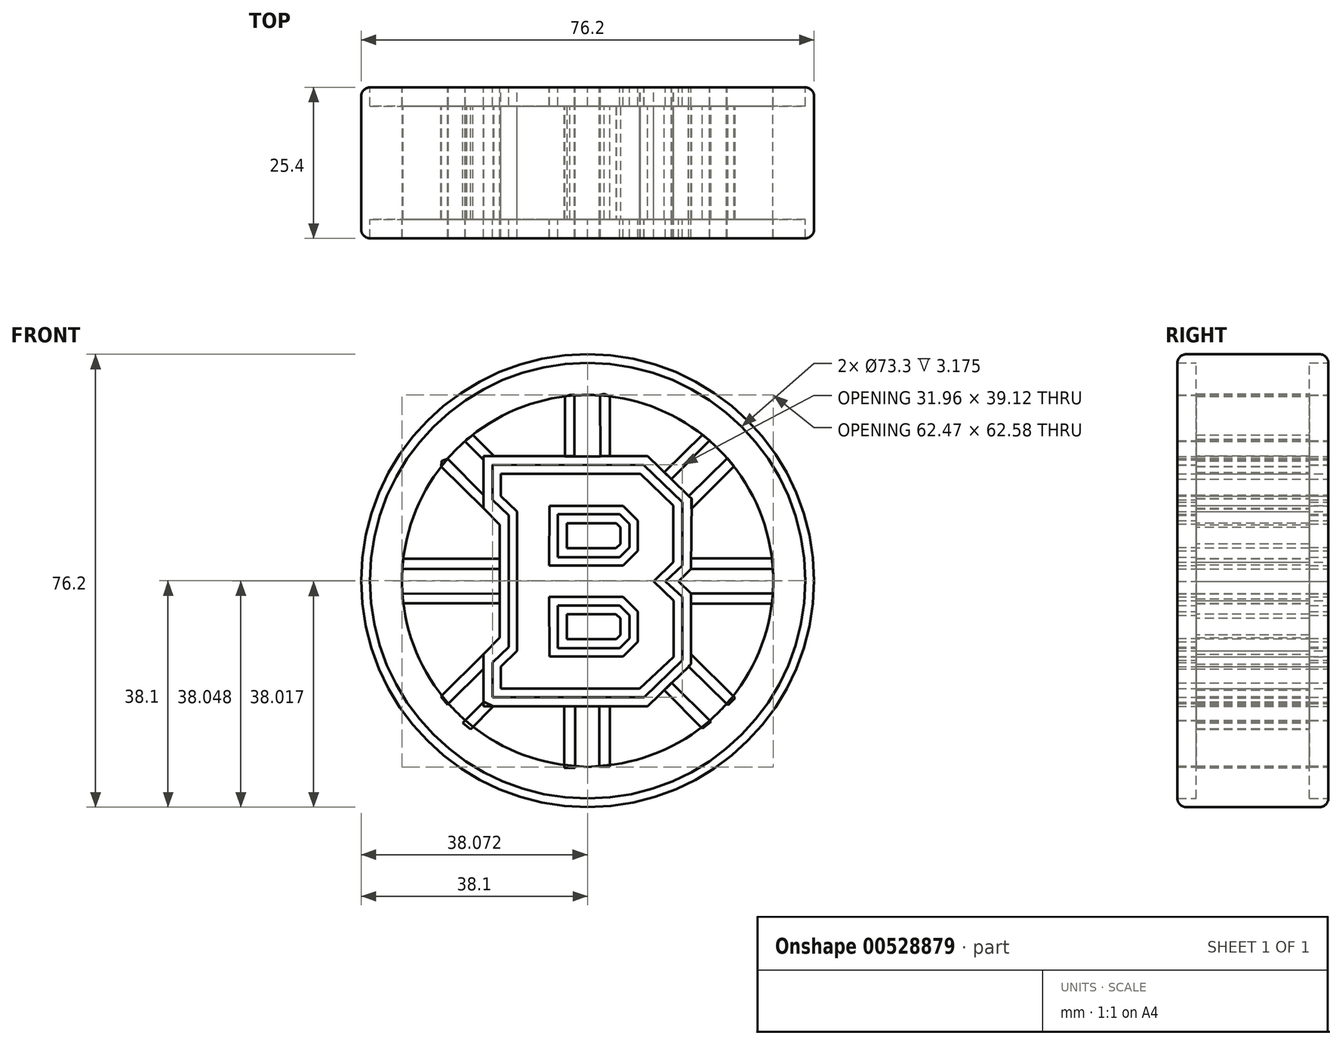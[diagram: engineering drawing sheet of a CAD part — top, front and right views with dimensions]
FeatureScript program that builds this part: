
annotation { "Feature Type Name" : "Feature", "Feature Type Description" : "" }
export const myFeature = defineFeature(function(context is Context, id is Id, definition is map)
    precondition{}
    {
        {
            var Q0;
            Q0=qCreatedBy(makeId("Front.planeOp"),FACE);
            var sketch = newSketch(context, id + "F0", { "sketchPlane" : qUnion([Q0])});
            skCircle(sketch, "E0", {"center": v(0, 0) * mm, "radius": 38.1 * mm});
            skCircle(sketch, "E1", {"center": v(0, 0) * mm, "radius": 36.65 * mm});
            skCircle(sketch, "E2", {"center": v(0, 0) * mm, "radius": 31.24 * mm});
            skSolve(sketch);
        }
        {
            var Q0;
            Q0=qCreatedBy(makeId("Front.planeOp"),FACE);
            var sketch = newSketch(context, id + "F1", { "sketchPlane" : qUnion([Q0])});
            skLineSegment(sketch, "E3", {"start": v(-3.5, 9.64) * mm, "end": v(-3.5, 5.5) * mm});
            skLineSegment(sketch, "E4", {"start": v(-3.5, 5.5) * mm, "end": v(4.78, 5.5) * mm});
            skLineSegment(sketch, "E5", {"start": v(4.78, 5.5) * mm, "end": v(5.5, 6.17) * mm});
            skLineSegment(sketch, "E6", {"start": v(5.5, 6.17) * mm, "end": v(5.5, 8.94) * mm});
            skLineSegment(sketch, "E7", {"start": v(5.5, 8.94) * mm, "end": v(4.82, 9.65) * mm});
            skLineSegment(sketch, "E8", {"start": v(4.82, 9.65) * mm, "end": v(-3.5, 9.64) * mm});
            skLineSegment(sketch, "E9.MirrorCS", {"start": v(5.5, -9.12) * mm, "end": v(4.82, -9.83) * mm});
            skLineSegment(sketch, "E10.MirrorCS", {"start": v(4.79, -5.67) * mm, "end": v(5.5, -6.35) * mm});
            skLineSegment(sketch, "E11.MirrorCS", {"start": v(4.82, -9.83) * mm, "end": v(-3.5, -9.82) * mm});
            skLineSegment(sketch, "E12.MirrorCS", {"start": v(5.5, -6.35) * mm, "end": v(5.5, -9.12) * mm});
            skLineSegment(sketch, "E13.MirrorCS", {"start": v(-3.5, -5.67) * mm, "end": v(4.79, -5.67) * mm});
            skLineSegment(sketch, "E14.MirrorCS", {"start": v(-3.5, -9.82) * mm, "end": v(-3.5, -5.67) * mm});
            skSolve(sketch);
        }
        {
            var Q0;
            Q0=makeQuery(id+"F0.imprint","IMPRINT",FACE,{"disambiguationData":[TD([[makeQuery(id+"F0.imprint","IMPRINT",EDGE,{"derivedFrom":sQuery(id+"F0.wireOp",EDGE,"E2")}),1.0]])]});
            var sketch = newSketch(context, id + "F2", { "sketchPlane" : qUnion([Q0])});
            skLineSegment(sketch, "E15", {"start": v(-5.02, 11.17) * mm, "end": v(-5.02, 3.97) * mm});
            skLineSegment(sketch, "E16", {"start": v(-5.02, 3.97) * mm, "end": v(5.41, 3.97) * mm});
            skLineSegment(sketch, "E17", {"start": v(5.41, 3.97) * mm, "end": v(7.05, 5.62) * mm});
            skLineSegment(sketch, "E18", {"start": v(7.05, 5.62) * mm, "end": v(7.05, 9.53) * mm});
            skLineSegment(sketch, "E19", {"start": v(7.05, 9.53) * mm, "end": v(5.4, 11.18) * mm});
            skLineSegment(sketch, "E20", {"start": v(5.4, 11.18) * mm, "end": v(-5.02, 11.17) * mm});
            skLineSegment(sketch, "E21", {"start": v(-6.44, 12.58) * mm, "end": v(5.96, 12.58) * mm});
            skLineSegment(sketch, "E22", {"start": v(5.96, 12.58) * mm, "end": v(8.43, 10.1) * mm});
            skLineSegment(sketch, "E23", {"start": v(8.43, 10.1) * mm, "end": v(8.43, 5.03) * mm});
            skLineSegment(sketch, "E24", {"start": v(8.43, 5.03) * mm, "end": v(5.94, 2.56) * mm});
            skLineSegment(sketch, "E25", {"start": v(5.94, 2.56) * mm, "end": v(-6.45, 2.56) * mm});
            skLineSegment(sketch, "E26", {"start": v(-6.45, 2.56) * mm, "end": v(-6.44, 12.58) * mm});
            skLineSegment(sketch, "E27.MirrorCS", {"start": v(5.96, -12.77) * mm, "end": v(8.43, -10.29) * mm});
            skLineSegment(sketch, "E28.MirrorCS", {"start": v(8.43, -10.29) * mm, "end": v(8.43, -5.22) * mm});
            skLineSegment(sketch, "E29.MirrorCS", {"start": v(-6.44, -12.77) * mm, "end": v(5.96, -12.77) * mm});
            skLineSegment(sketch, "E30.MirrorCS", {"start": v(-5.02, -4.16) * mm, "end": v(5.41, -4.16) * mm});
            skLineSegment(sketch, "E31.MirrorCS", {"start": v(5.4, -11.37) * mm, "end": v(-5.02, -11.36) * mm});
            skLineSegment(sketch, "E32.MirrorCS", {"start": v(7.05, -9.72) * mm, "end": v(5.4, -11.37) * mm});
            skLineSegment(sketch, "E33.MirrorCS", {"start": v(5.41, -4.16) * mm, "end": v(7.05, -5.81) * mm});
            skLineSegment(sketch, "E34.MirrorCS", {"start": v(-6.45, -2.75) * mm, "end": v(-6.44, -12.77) * mm});
            skLineSegment(sketch, "E35.MirrorCS", {"start": v(5.94, -2.75) * mm, "end": v(-6.45, -2.75) * mm});
            skLineSegment(sketch, "E36.MirrorCS", {"start": v(-5.02, -11.36) * mm, "end": v(-5.02, -4.16) * mm});
            skLineSegment(sketch, "E37.MirrorCS", {"start": v(7.05, -5.81) * mm, "end": v(7.05, -9.72) * mm});
            skLineSegment(sketch, "E38.MirrorCS", {"start": v(8.43, -5.22) * mm, "end": v(5.94, -2.75) * mm});
            skSolve(sketch);
        }
        {
            var Q0;
            Q0=makeQuery(id+"F2.imprint","IMPRINT",FACE,{"disambiguationData":[TD([[makeQuery(id+"F2.imprint","IMPRINT",EDGE,{"derivedFrom":sQuery(id+"F2.wireOp",EDGE,"E30.MirrorCS")}),-1.0]])]});
            var Q1;
            Q1 = qSketchRegion(id + "F1", true);
            var Q2;
            Q2=makeQuery(id+"F2.imprint","IMPRINT",FACE,{"disambiguationData":[TD([[makeQuery(id+"F2.imprint","IMPRINT",EDGE,{"derivedFrom":sQuery(id+"F2.wireOp",EDGE,"E15")}),1.0]])]});
            var Q3;
            Q3 = qSketchRegion(id + "F4", true);
            extrude(context, id + "F3", {"entities" : qUnion([Q0, Q1, Q2, Q3]), "depth" : 19.05 * mm, "offsetDistance" : 25 * mm, "symmetric" : true});
        }
        {
            var Q0;
            Q0=qCreatedBy(makeId("Front.planeOp"),FACE);
            var sketch = newSketch(context, id + "F4", { "sketchPlane" : qUnion([Q0])});
            skLineSegment(sketch, "E39", {"start": v(-14.6, 18) * mm, "end": v(-14.6, 14.24) * mm});
            skLineSegment(sketch, "E40", {"start": v(-14.6, 14.24) * mm, "end": v(-11.85, 11.62) * mm});
            skLineSegment(sketch, "E41", {"start": v(-11.85, 11.62) * mm, "end": v(-11.85, -11.81) * mm});
            skLineSegment(sketch, "E42", {"start": v(-11.85, -11.81) * mm, "end": v(-14.6, -14.46) * mm});
            skLineSegment(sketch, "E43", {"start": v(-14.6, -14.46) * mm, "end": v(-14.6, -18.18) * mm});
            skLineSegment(sketch, "E44", {"start": v(-14.6, -18.18) * mm, "end": v(8.77, -18.18) * mm});
            skLineSegment(sketch, "E45", {"start": v(8.77, -18.18) * mm, "end": v(14.49, -12.83) * mm});
            skLineSegment(sketch, "E46", {"start": v(14.49, -12.83) * mm, "end": v(14.49, -3.38) * mm});
            skLineSegment(sketch, "E47", {"start": v(14.44, 3.14) * mm, "end": v(14.43, 12.62) * mm});
            skLineSegment(sketch, "E48", {"start": v(14.43, 12.62) * mm, "end": v(8.89, 18) * mm});
            skLineSegment(sketch, "E49", {"start": v(8.89, 18) * mm, "end": v(-14.6, 18) * mm});
            skLineSegment(sketch, "E50", {"start": v(11.09, -0.12) * mm, "end": v(14.49, -3.38) * mm});
            skLineSegment(sketch, "E51", {"start": v(11.09, -0.12) * mm, "end": v(14.44, 3.14) * mm});
            skLineSegment(sketch, "E52", {"start": v(-16, 19.48) * mm, "end": v(-16, 13.6) * mm});
            skLineSegment(sketch, "E53", {"start": v(-16, 13.6) * mm, "end": v(-13.3, 11) * mm});
            skLineSegment(sketch, "E54", {"start": v(-13.3, 11) * mm, "end": v(-13.3, -11.18) * mm});
            skLineSegment(sketch, "E55", {"start": v(-13.3, -11.18) * mm, "end": v(-16, -13.79) * mm});
            skLineSegment(sketch, "E56", {"start": v(-16, -13.79) * mm, "end": v(-16, -19.64) * mm});
            skLineSegment(sketch, "E57", {"start": v(-16, -19.64) * mm, "end": v(9.5, -19.64) * mm});
            skLineSegment(sketch, "E58", {"start": v(9.5, -19.64) * mm, "end": v(15.9, -13.42) * mm});
            skLineSegment(sketch, "E59", {"start": v(15.9, -13.42) * mm, "end": v(15.9, -2.75) * mm});
            skLineSegment(sketch, "E60", {"start": v(15.95, 2.52) * mm, "end": v(15.9, 13.2) * mm});
            skLineSegment(sketch, "E61", {"start": v(15.9, 13.2) * mm, "end": v(9.47, 19.46) * mm});
            skLineSegment(sketch, "E62", {"start": v(9.47, 19.46) * mm, "end": v(-16, 19.48) * mm});
            skLineSegment(sketch, "E63", {"start": v(13.1, -0.1) * mm, "end": v(15.9, -2.75) * mm});
            skLineSegment(sketch, "E64", {"start": v(13.1, -0.1) * mm, "end": v(15.95, 2.52) * mm});
            skLineSegment(sketch, "E65", {"start": v(-17.55, 20.98) * mm, "end": v(-17.55, 12.22) * mm});
            skLineSegment(sketch, "E66", {"start": v(-17.55, 12.22) * mm, "end": v(-14.82, 9.4) * mm});
            skLineSegment(sketch, "E67", {"start": v(-14.82, 9.4) * mm, "end": v(-14.82, -9.59) * mm});
            skLineSegment(sketch, "E68", {"start": v(-14.82, -9.59) * mm, "end": v(-17.55, -12.34) * mm});
            skLineSegment(sketch, "E69", {"start": v(-17.55, -12.34) * mm, "end": v(-17.55, -21.15) * mm});
            skLineSegment(sketch, "E70", {"start": v(-17.55, -21.15) * mm, "end": v(10.1, -21.15) * mm});
            skLineSegment(sketch, "E71", {"start": v(10.1, -21.15) * mm, "end": v(17.4, -14.05) * mm});
            skLineSegment(sketch, "E72", {"start": v(17.4, -14.05) * mm, "end": v(17.4, -2.13) * mm});
            skLineSegment(sketch, "E73", {"start": v(17.4, 1.95) * mm, "end": v(17.53, 13.76) * mm});
            skLineSegment(sketch, "E74", {"start": v(17.53, 13.76) * mm, "end": v(10.12, 20.96) * mm});
            skLineSegment(sketch, "E75", {"start": v(10.12, 20.96) * mm, "end": v(-17.55, 20.98) * mm});
            skLineSegment(sketch, "E76", {"start": v(15.33, -0.1) * mm, "end": v(17.4, -2.13) * mm});
            skLineSegment(sketch, "E77", {"start": v(15.33, -0.1) * mm, "end": v(17.4, 1.95) * mm});
            skSolve(sketch);
        }
        {
            var Q0;
            Q0=qCreatedBy(makeId("Front.planeOp"),FACE);
            var sketch = newSketch(context, id + "F5", { "sketchPlane" : qUnion([Q0])});
            skLineSegment(sketch, "E78", {"start": v(-14.58, 17.99) * mm, "end": v(-14.58, 14.28) * mm});
            skLineSegment(sketch, "E79", {"start": v(-14.58, 14.28) * mm, "end": v(-11.8, 11.63) * mm});
            skLineSegment(sketch, "E80", {"start": v(-11.8, 11.63) * mm, "end": v(-11.8, -11.85) * mm});
            skLineSegment(sketch, "E81", {"start": v(-11.8, -11.85) * mm, "end": v(-14.58, -14.46) * mm});
            skLineSegment(sketch, "E82", {"start": v(-14.58, -14.46) * mm, "end": v(-14.58, -18.17) * mm});
            skLineSegment(sketch, "E83", {"start": v(-14.58, -18.17) * mm, "end": v(8.94, -18.17) * mm});
            skLineSegment(sketch, "E84", {"start": v(8.94, -18.17) * mm, "end": v(14.46, -12.8) * mm});
            skLineSegment(sketch, "E85", {"start": v(14.46, -12.8) * mm, "end": v(14.46, -3.44) * mm});
            skLineSegment(sketch, "E86", {"start": v(14.44, 3.2) * mm, "end": v(14.46, 12.59) * mm});
            skLineSegment(sketch, "E87", {"start": v(14.46, 12.59) * mm, "end": v(8.88, 18.02) * mm});
            skLineSegment(sketch, "E88", {"start": v(8.88, 18.02) * mm, "end": v(-14.58, 17.99) * mm});
            skLineSegment(sketch, "E89", {"start": v(11.07, -0.1) * mm, "end": v(14.46, -3.44) * mm});
            skLineSegment(sketch, "E90", {"start": v(11.07, -0.1) * mm, "end": v(14.44, 3.2) * mm});
            skSolve(sketch);
        }
        {
            var Q0;
            Q0 = qSketchRegion(id + "F4", true);
            extrude(context, id + "F6", {"entities" : qUnion([Q0]), "depth" : 19.05 * mm, "offsetDistance" : 25 * mm, "symmetric" : true});
        }
        {
            var Q0;
            Q0=makeQuery(id+"F4.imprint","IMPRINT",FACE,{"disambiguationData":[TD([[makeQuery(id+"F4.imprint","IMPRINT",EDGE,{"derivedFrom":sQuery(id+"F4.wireOp",EDGE,"E39")}),-1.0]])]});
            var Q1;
            Q1 = qConstructionFilter(qBodyType(qCreatedBy(id + "F5" ,EDGE), BodyType.WIRE), ConstructionObject.NO);
            var Q2;
            Q2=sQuery(id+"F4.wireOp",EDGE,"E56");
            var Q3;
            Q3=sQuery(id+"F4.wireOp",EDGE,"E55");
            var Q4;
            Q4=sQuery(id+"F4.wireOp",EDGE,"E54");
            var Q5;
            Q5=sQuery(id+"F4.wireOp",EDGE,"E57");
            var Q6;
            Q6=sQuery(id+"F4.wireOp",EDGE,"E58");
            var Q7;
            Q7=sQuery(id+"F4.wireOp",EDGE,"E59");
            var Q8;
            Q8=sQuery(id+"F4.wireOp",EDGE,"E64");
            var Q9;
            Q9=sQuery(id+"F4.wireOp",EDGE,"E63");
            var Q10;
            Q10=sQuery(id+"F4.wireOp",EDGE,"E60");
            var Q11;
            Q11=sQuery(id+"F4.wireOp",EDGE,"E61");
            var Q12;
            Q12=sQuery(id+"F4.wireOp",EDGE,"E62");
            var Q13;
            Q13=sQuery(id+"F4.wireOp",EDGE,"E52");
            var Q14;
            Q14=sQuery(id+"F4.wireOp",EDGE,"E53");
            extrude(context, id + "F7", {"entities" : qUnion([Q0]), "operationType" : NewBodyOperationType.ADD, "surfaceEntities" : qUnion([Q1, Q2, Q3, Q4, Q5, Q6, Q7, Q8, Q9, Q10, Q11, Q12, Q13, Q14]), "depth" : 25.4 * mm, "offsetDistance" : 25 * mm, "symmetric" : true});
        }
        {
            var Q0;
            Q0=makeQuery(id+"F4.imprint","IMPRINT",FACE,{"disambiguationData":[TD([[makeQuery(id+"F4.imprint","IMPRINT",EDGE,{"derivedFrom":sQuery(id+"F4.wireOp",EDGE,"E39")}),1.0]])]});
            extrude(context, id + "F8", {"entities" : qUnion([Q0]), "depth" : 19.05 * mm, "offsetDistance" : 25 * mm, "symmetric" : true});
        }
        {
            var Q0;
            Q0=makeQuery(id+"F1.imprint","IMPRINT",FACE,{"disambiguationData":[TD([[makeQuery(id+"F1.imprint","IMPRINT",EDGE,{"derivedFrom":sQuery(id+"F1.wireOp",EDGE,"E3")}),1.0]])]});
            var Q1;
            Q1=makeQuery(id+"F1.imprint","IMPRINT",FACE,{"disambiguationData":[TD([[makeQuery(id+"F1.imprint","IMPRINT",EDGE,{"derivedFrom":sQuery(id+"F1.wireOp",EDGE,"E9.MirrorCS")}),-1.0]])]});
            extrude(context, id + "F9", {"entities" : qUnion([Q0, Q1]), "operationType" : NewBodyOperationType.REMOVE, "oppositeDirection" : true, "depth" : 25.4 * mm, "offsetDistance" : 25 * mm, "symmetric" : true});
        }
        {
            var Q0;
            Q0=makeQuery(id+"F0.imprint","IMPRINT",FACE,{"disambiguationData":[TD([[makeQuery(id+"F0.imprint","IMPRINT",EDGE,{"derivedFrom":sQuery(id+"F0.wireOp",EDGE,"E0")}),1.0]])]});
            var Q1;
            Q1=sQuery(id+"F0.wireOp",EDGE,"E0");
            extrude(context, id + "F10", {"entities" : qUnion([Q0]), "surfaceEntities" : qUnion([Q1]), "depth" : 25.4 * mm, "offsetDistance" : 25 * mm, "symmetric" : true});
        }
        {
            var Q0;
            Q0=makeQuery(id+"F0.imprint","IMPRINT",FACE,{"disambiguationData":[TD([[makeQuery(id+"F0.imprint","IMPRINT",EDGE,{"derivedFrom":sQuery(id+"F0.wireOp",EDGE,"E1")}),1.0]])]});
            extrude(context, id + "F11", {"entities" : qUnion([Q0]), "operationType" : NewBodyOperationType.ADD, "depth" : 19.05 * mm, "offsetDistance" : 25 * mm, "symmetric" : true});
        }
        {
            var Q0;
            Q0=qCreatedBy(makeId("Front.planeOp"),FACE);
            var sketch = newSketch(context, id + "F12", { "sketchPlane" : qUnion([Q0]), "disableImprinting" : false});
            skLineSegment(sketch, "E91", {"start": v(-31.05, 3.67) * mm, "end": v(-14.82, 3.67) * mm});
            skLineSegment(sketch, "E92", {"start": v(-14.82, 3.67) * mm, "end": v(-14.82, 2) * mm});
            skLineSegment(sketch, "E93", {"start": v(-14.82, 2) * mm, "end": v(-31.17, 2) * mm});
            skLineSegment(sketch, "E94", {"start": v(-31.17, 2) * mm, "end": v(-31.17, 2.7) * mm});
            skLineSegment(sketch, "E95", {"start": v(-31.17, 2.7) * mm, "end": v(-31.05, 3.67) * mm});
            skLineSegment(sketch, "E96", {"start": v(-31.17, -2.16) * mm, "end": v(-31.17, -3) * mm});
            skLineSegment(sketch, "E97", {"start": v(-31.17, -3) * mm, "end": v(-31.05, -3.81) * mm});
            skLineSegment(sketch, "E98", {"start": v(-31.05, -3.81) * mm, "end": v(-14.82, -3.81) * mm});
            skLineSegment(sketch, "E99", {"start": v(-14.82, -3.81) * mm, "end": v(-14.82, -2.2) * mm});
            skLineSegment(sketch, "E100", {"start": v(-14.82, -2.2) * mm, "end": v(-31.17, -2.16) * mm});
            skLineSegment(sketch, "E101", {"start": v(-24.64, 19.2) * mm, "end": v(-17.55, 12.22) * mm});
            skLineSegment(sketch, "E102", {"start": v(-17.55, 12.22) * mm, "end": v(-17.55, 14.45) * mm});
            skLineSegment(sketch, "E103", {"start": v(-17.55, 14.45) * mm, "end": v(-23.58, 20.5) * mm});
            skLineSegment(sketch, "E104", {"start": v(-17.55, 20.33) * mm, "end": v(-17.55, 20.98) * mm});
            skLineSegment(sketch, "E105", {"start": v(-17.55, 20.98) * mm, "end": v(-15.74, 20.98) * mm});
            skLineSegment(sketch, "E106", {"start": v(-15.74, 20.98) * mm, "end": v(-19.33, 24.53) * mm});
            skLineSegment(sketch, "E107", {"start": v(-19.33, 24.53) * mm, "end": v(-20.34, 23.82) * mm});
            skLineSegment(sketch, "E108", {"start": v(-20.34, 23.82) * mm, "end": v(-20.63, 23.47) * mm});
            skLineSegment(sketch, "E109", {"start": v(-20.63, 23.47) * mm, "end": v(-17.55, 20.33) * mm});
            skLineSegment(sketch, "E110", {"start": v(-3.83, 31) * mm, "end": v(-2.96, 31.28) * mm});
            skLineSegment(sketch, "E111", {"start": v(-2.96, 31.28) * mm, "end": v(-2.21, 31.28) * mm});
            skLineSegment(sketch, "E112", {"start": v(-2.21, 31.28) * mm, "end": v(-2.21, 20.9) * mm});
            skLineSegment(sketch, "E113", {"start": v(-2.21, 20.9) * mm, "end": v(-3.8, 20.9) * mm});
            skLineSegment(sketch, "E114", {"start": v(-3.8, 20.9) * mm, "end": v(-3.83, 31) * mm});
            skLineSegment(sketch, "E115", {"start": v(2.12, 31.26) * mm, "end": v(2.8, 31.47) * mm});
            skLineSegment(sketch, "E116", {"start": v(2.8, 31.47) * mm, "end": v(3.77, 31) * mm});
            skLineSegment(sketch, "E117", {"start": v(3.77, 31) * mm, "end": v(3.77, 20.97) * mm});
            skLineSegment(sketch, "E118", {"start": v(3.77, 20.97) * mm, "end": v(2.15, 20.97) * mm});
            skLineSegment(sketch, "E119", {"start": v(2.15, 20.97) * mm, "end": v(2.12, 31.26) * mm});
            skLineSegment(sketch, "E120", {"start": v(12.87, 18.24) * mm, "end": v(19.33, 24.54) * mm});
            skLineSegment(sketch, "E121", {"start": v(19.33, 24.54) * mm, "end": v(20.55, 23.6) * mm});
            skLineSegment(sketch, "E122", {"start": v(20.55, 23.6) * mm, "end": v(14.08, 17.08) * mm});
            skLineSegment(sketch, "E123", {"start": v(14.08, 17.08) * mm, "end": v(12.87, 18.24) * mm});
            skLineSegment(sketch, "E124", {"start": v(17.03, 14.25) * mm, "end": v(23.54, 20.62) * mm});
            skLineSegment(sketch, "E125", {"start": v(23.54, 20.62) * mm, "end": v(24.64, 19.26) * mm});
            skLineSegment(sketch, "E126", {"start": v(24.64, 19.26) * mm, "end": v(17.44, 12.1) * mm});
            skLineSegment(sketch, "E127", {"start": v(17.44, 12.1) * mm, "end": v(17.44, 13.85) * mm});
            skLineSegment(sketch, "E128", {"start": v(17.44, 13.85) * mm, "end": v(17.03, 14.25) * mm});
            skLineSegment(sketch, "E129.bottom", {"start": v(17.4, 3.73) * mm, "end": v(31.18, 3.73) * mm});
            skLineSegment(sketch, "E129.top", {"start": v(17.4, 1.95) * mm, "end": v(31.18, 1.95) * mm});
            skLineSegment(sketch, "E129.left", {"start": v(17.4, 3.73) * mm, "end": v(17.4, 1.95) * mm});
            skLineSegment(sketch, "E129.right", {"start": v(31.18, 3.73) * mm, "end": v(31.18, 1.95) * mm});
            skLineSegment(sketch, "E130.bottom", {"start": v(17.37, -2.13) * mm, "end": v(31.16, -2.13) * mm});
            skLineSegment(sketch, "E130.top", {"start": v(17.37, -3.86) * mm, "end": v(31.16, -3.86) * mm});
            skLineSegment(sketch, "E130.left", {"start": v(17.37, -2.13) * mm, "end": v(17.37, -3.86) * mm});
            skLineSegment(sketch, "E130.right", {"start": v(31.16, -2.13) * mm, "end": v(31.16, -3.86) * mm});
            skLineSegment(sketch, "E131.bottom", {"start": v(-3.95, -21.15) * mm, "end": v(-2.08, -21.15) * mm});
            skLineSegment(sketch, "E131.top", {"start": v(-3.95, -31.46) * mm, "end": v(-2.08, -31.46) * mm});
            skLineSegment(sketch, "E131.left", {"start": v(-3.95, -21.15) * mm, "end": v(-3.95, -31.46) * mm});
            skLineSegment(sketch, "E131.right", {"start": v(-2.08, -21.15) * mm, "end": v(-2.08, -31.46) * mm});
            skLineSegment(sketch, "E132.bottom", {"start": v(1.94, -21.12) * mm, "end": v(3.75, -21.12) * mm});
            skLineSegment(sketch, "E132.top", {"start": v(1.94, -31.28) * mm, "end": v(3.75, -31.28) * mm});
            skLineSegment(sketch, "E132.left", {"start": v(1.94, -21.12) * mm, "end": v(1.94, -31.28) * mm});
            skLineSegment(sketch, "E132.right", {"start": v(3.75, -21.12) * mm, "end": v(3.75, -31.28) * mm});
            skLineSegment(sketch, "E133", {"start": v(12.88, -18.42) * mm, "end": v(14.12, -17.2) * mm});
            skLineSegment(sketch, "E134", {"start": v(14.12, -17.2) * mm, "end": v(20.75, -23.72) * mm});
            skLineSegment(sketch, "E135", {"start": v(20.75, -23.72) * mm, "end": v(19.32, -24.9) * mm});
            skLineSegment(sketch, "E136", {"start": v(19.32, -24.9) * mm, "end": v(12.88, -18.42) * mm});
            skLineSegment(sketch, "E137", {"start": v(17.38, -12.34) * mm, "end": v(17.38, -14.04) * mm});
            skLineSegment(sketch, "E138", {"start": v(17.38, -14.04) * mm, "end": v(16.96, -14.4) * mm});
            skLineSegment(sketch, "E139", {"start": v(16.96, -14.4) * mm, "end": v(23.64, -20.94) * mm});
            skLineSegment(sketch, "E140", {"start": v(23.64, -20.94) * mm, "end": v(24.8, -19.75) * mm});
            skLineSegment(sketch, "E141", {"start": v(24.8, -19.75) * mm, "end": v(17.38, -12.34) * mm});
            skLineSegment(sketch, "E142", {"start": v(-24.68, -19.48) * mm, "end": v(-17.55, -12.34) * mm});
            skLineSegment(sketch, "E143", {"start": v(-17.55, -12.34) * mm, "end": v(-17.55, -14.83) * mm});
            skLineSegment(sketch, "E144", {"start": v(-17.55, -14.83) * mm, "end": v(-23.57, -20.85) * mm});
            skLineSegment(sketch, "E145", {"start": v(-23.57, -20.85) * mm, "end": v(-24.68, -19.48) * mm});
            skLineSegment(sketch, "E146", {"start": v(-21, -23.9) * mm, "end": v(-17.47, -20.38) * mm});
            skLineSegment(sketch, "E147", {"start": v(-17.47, -20.38) * mm, "end": v(-15.84, -21.15) * mm});
            skLineSegment(sketch, "E148", {"start": v(-15.84, -21.15) * mm, "end": v(-19.7, -25) * mm});
            skLineSegment(sketch, "E149", {"start": v(-19.7, -25) * mm, "end": v(-21, -23.9) * mm});
            skLineSegment(sketch, "E150", {"start": v(-24.64, 19.2) * mm, "end": v(-24.56, 20.11) * mm});
            skLineSegment(sketch, "E151", {"start": v(-24.56, 20.11) * mm, "end": v(-23.58, 20.5) * mm});
            skSolve(sketch);
        }
        {
            var Q0;
            Q0=qCreatedBy(makeId("Front.planeOp"),FACE);
            var sketch = newSketch(context, id + "F13", { "sketchPlane" : qUnion([Q0])});
            skLineSegment(sketch, "E152", {"start": v(-31.17, -2.16) * mm, "end": v(-14.8, -2.2) * mm});
            skLineSegment(sketch, "E153", {"start": v(-14.8, 2) * mm, "end": v(-31.17, 2) * mm});
            skLineSegment(sketch, "E154", {"start": v(-14.8, 2) * mm, "end": v(-14.8, -2.2) * mm});
            skLineSegment(sketch, "E155", {"start": v(-17.55, -14.83) * mm, "end": v(-17.55, -20.46) * mm});
            skLineSegment(sketch, "E156", {"start": v(-17.55, -20.46) * mm, "end": v(-20.61, -23.52) * mm});
            skLineSegment(sketch, "E157", {"start": v(-23.42, -20.7) * mm, "end": v(-17.55, -14.83) * mm});
            skLineSegment(sketch, "E158", {"start": v(-23.42, -20.7) * mm, "end": v(-21.04, -23.39) * mm});
            skLineSegment(sketch, "E159", {"start": v(-21.04, -23.39) * mm, "end": v(-20.61, -23.52) * mm});
            skLineSegment(sketch, "E160", {"start": v(-2.08, -21.15) * mm, "end": v(-2.08, -31.18) * mm});
            skLineSegment(sketch, "E161", {"start": v(-2.08, -31.18) * mm, "end": v(0, -31.34) * mm});
            skLineSegment(sketch, "E162", {"start": v(0, -31.34) * mm, "end": v(1.94, -31.18) * mm});
            skLineSegment(sketch, "E163", {"start": v(1.94, -31.18) * mm, "end": v(1.94, -21.15) * mm});
            skLineSegment(sketch, "E164", {"start": v(1.94, -21.15) * mm, "end": v(-2.08, -21.15) * mm});
            skLineSegment(sketch, "E165", {"start": v(14.14, -17.22) * mm, "end": v(20.55, -23.52) * mm});
            skLineSegment(sketch, "E166", {"start": v(20.55, -23.52) * mm, "end": v(22.72, -22.85) * mm});
            skLineSegment(sketch, "E167", {"start": v(22.72, -22.85) * mm, "end": v(23.4, -20.7) * mm});
            skLineSegment(sketch, "E168", {"start": v(23.4, -20.7) * mm, "end": v(17, -14.44) * mm});
            skLineSegment(sketch, "E169", {"start": v(17, -14.44) * mm, "end": v(14.14, -17.22) * mm});
            skLineSegment(sketch, "E170", {"start": v(15.33, -0.1) * mm, "end": v(17.4, -2.13) * mm});
            skLineSegment(sketch, "E171", {"start": v(17.4, -2.13) * mm, "end": v(31.16, -2.13) * mm});
            skLineSegment(sketch, "E172", {"start": v(31.16, -2.13) * mm, "end": v(31.94, 0) * mm});
            skLineSegment(sketch, "E173", {"start": v(31.94, 0) * mm, "end": v(31.94, 1.95) * mm});
            skLineSegment(sketch, "E174", {"start": v(31.94, 1.95) * mm, "end": v(17.4, 1.95) * mm});
            skLineSegment(sketch, "E175", {"start": v(17.4, 1.95) * mm, "end": v(15.33, -0.1) * mm});
            skLineSegment(sketch, "E176", {"start": v(14.1, 17.1) * mm, "end": v(21.06, 24.1) * mm});
            skLineSegment(sketch, "E177", {"start": v(21.06, 24.1) * mm, "end": v(22.54, 22.64) * mm});
            skLineSegment(sketch, "E178", {"start": v(22.54, 22.64) * mm, "end": v(24.05, 21.1) * mm});
            skLineSegment(sketch, "E179", {"start": v(24.05, 21.1) * mm, "end": v(17.03, 14.25) * mm});
            skLineSegment(sketch, "E180", {"start": v(17.03, 14.25) * mm, "end": v(14.1, 17.1) * mm});
            skLineSegment(sketch, "E181", {"start": v(-2.21, 31.16) * mm, "end": v(-2.21, 20.9) * mm});
            skLineSegment(sketch, "E182", {"start": v(-2.21, 20.9) * mm, "end": v(2.15, 20.9) * mm});
            skLineSegment(sketch, "E183", {"start": v(2.15, 20.9) * mm, "end": v(2.12, 31.16) * mm});
            skLineSegment(sketch, "E184", {"start": v(2.12, 31.16) * mm, "end": v(0, 32.1) * mm});
            skLineSegment(sketch, "E185", {"start": v(0, 32.1) * mm, "end": v(-2.21, 31.16) * mm});
            skLineSegment(sketch, "E186", {"start": v(-23.58, 20.5) * mm, "end": v(-17.55, 14.45) * mm});
            skLineSegment(sketch, "E187", {"start": v(-17.55, 14.45) * mm, "end": v(-17.55, 20.33) * mm});
            skLineSegment(sketch, "E188", {"start": v(-17.55, 20.33) * mm, "end": v(-21.7, 24.56) * mm});
            skLineSegment(sketch, "E189", {"start": v(-21.7, 24.56) * mm, "end": v(-23.49, 22.8) * mm});
            skLineSegment(sketch, "E190", {"start": v(-23.49, 22.8) * mm, "end": v(-23.58, 20.5) * mm});
            skCircle(sketch, "E191.0", {"center": v(0, 0) * mm, "radius": 31.24 * mm});
            skSolve(sketch);
        }
        {
            var Q0;
            Q0=makeQuery(id+"F13.imprint","IMPRINT",FACE,{"disambiguationData":[TD([[makeQuery(id+"F13.imprint","IMPRINT",EDGE,{"derivedFrom":sQuery(id+"F13.wireOp",EDGE,"E152")}),1.0]])]});
            var Q1;
            Q1=makeQuery(id+"F13.imprint","IMPRINT",FACE,{"disambiguationData":[TD([[makeQuery(id+"F13.imprint","IMPRINT",EDGE,{"derivedFrom":sQuery(id+"F13.wireOp",EDGE,"E155")}),-1.0]])]});
            var Q2;
            Q2=makeQuery(id+"F13.imprint","IMPRINT",FACE,{"disambiguationData":[TD([[makeQuery(id+"F13.imprint","IMPRINT",EDGE,{"derivedFrom":sQuery(id+"F13.wireOp",EDGE,"E160")}),1.0]])]});
            var Q3;
            Q3=makeQuery(id+"F13.imprint","IMPRINT",FACE,{"disambiguationData":[TD([[makeQuery(id+"F13.imprint","IMPRINT",EDGE,{"derivedFrom":sQuery(id+"F13.wireOp",EDGE,"E165")}),1.0]])]});
            var Q4;
            Q4=makeQuery(id+"F13.imprint","IMPRINT",FACE,{"disambiguationData":[TD([[makeQuery(id+"F13.imprint","IMPRINT",EDGE,{"derivedFrom":sQuery(id+"F13.wireOp",EDGE,"E170")}),1.0]])]});
            var Q5;
            Q5=makeQuery(id+"F13.imprint","IMPRINT",FACE,{"disambiguationData":[TD([[makeQuery(id+"F13.imprint","IMPRINT",EDGE,{"derivedFrom":sQuery(id+"F13.wireOp",EDGE,"E176")}),-1.0]])]});
            var Q6;
            Q6=makeQuery(id+"F13.imprint","IMPRINT",FACE,{"disambiguationData":[TD([[makeQuery(id+"F13.imprint","IMPRINT",EDGE,{"derivedFrom":sQuery(id+"F13.wireOp",EDGE,"E181")}),1.0]])]});
            var Q7;
            Q7=makeQuery(id+"F13.imprint","IMPRINT",FACE,{"disambiguationData":[TD([[makeQuery(id+"F13.imprint","IMPRINT",EDGE,{"derivedFrom":sQuery(id+"F13.wireOp",EDGE,"E186")}),1.0]])]});
            extrude(context, id + "F14", {"entities" : qUnion([Q0, Q1, Q2, Q3, Q4, Q5, Q6, Q7]), "operationType" : NewBodyOperationType.ADD, "depth" : 25.4 * mm, "offsetDistance" : 25 * mm, "symmetric" : true});
        }
        {
            var Q0;
            Q0 = qSketchRegion(id + "F12", true);
            extrude(context, id + "F15", {"entities" : qUnion([Q0]), "depth" : 19.05 * mm, "offsetDistance" : 25 * mm, "symmetric" : true});
        }
        {
            var Q0;
            Q0 = qSketchRegion(id + "F2", true);
            var Q1;
            Q1=sQuery(id+"F2.wireOp",EDGE,"E36.MirrorCS");
            var Q2;
            Q2=sQuery(id+"F2.wireOp",EDGE,"E32.MirrorCS");
            var Q3;
            Q3=sQuery(id+"F2.wireOp",EDGE,"E31.MirrorCS");
            var Q4;
            Q4=sQuery(id+"F1.wireOp",EDGE,"E11.MirrorCS");
            var Q5;
            Q5=sQuery(id+"F1.wireOp",EDGE,"E12.MirrorCS");
            var Q6;
            Q6=sQuery(id+"F1.wireOp",EDGE,"E9.MirrorCS");
            var Q7;
            Q7=sQuery(id+"F1.wireOp",EDGE,"E10.MirrorCS");
            var Q8;
            Q8=sQuery(id+"F1.wireOp",EDGE,"E13.MirrorCS");
            var Q9;
            Q9=sQuery(id+"F1.wireOp",EDGE,"E14.MirrorCS");
            var Q10;
            Q10=sQuery(id+"F2.wireOp",EDGE,"E30.MirrorCS");
            var Q11;
            Q11=sQuery(id+"F2.wireOp",EDGE,"E33.MirrorCS");
            var Q12;
            Q12=sQuery(id+"F2.wireOp",EDGE,"E37.MirrorCS");
            var Q13;
            Q13=sQuery(id+"F2.wireOp",EDGE,"E17");
            var Q14;
            Q14=sQuery(id+"F2.wireOp",EDGE,"E16");
            var Q15;
            Q15=sQuery(id+"F2.wireOp",EDGE,"E20");
            var Q16;
            Q16=sQuery(id+"F2.wireOp",EDGE,"E15");
            var Q17;
            Q17=sQuery(id+"F1.wireOp",EDGE,"E5");
            var Q18;
            Q18=sQuery(id+"F1.wireOp",EDGE,"E3");
            var Q19;
            Q19=sQuery(id+"F1.wireOp",EDGE,"E8");
            var Q20;
            Q20=sQuery(id+"F1.wireOp",EDGE,"E4");
            var Q21;
            Q21=sQuery(id+"F1.wireOp",EDGE,"E6");
            var Q22;
            Q22=sQuery(id+"F2.wireOp",EDGE,"E19");
            var Q23;
            Q23=sQuery(id+"F2.wireOp",EDGE,"E18");
            var Q24;
            Q24=sQuery(id+"F1.wireOp",EDGE,"E7");
            extrude(context, id + "F16", {"entities" : qUnion([Q0]), "operationType" : NewBodyOperationType.ADD, "surfaceEntities" : qUnion([Q1, Q2, Q3, Q4, Q5, Q6, Q7, Q8, Q9, Q10, Q11, Q12, Q13, Q14, Q15, Q16, Q17, Q18, Q19, Q20, Q21, Q22, Q23, Q24]), "depth" : 25.4 * mm, "offsetDistance" : 25 * mm, "symmetric" : true});
        }
        {
            var Q0;
            Q0=makeQuery(id+"F10.opExtrude","CAP_EDGE",EDGE,{"disambiguationData":[OSD([sQuery(id+"F0.wireOp",EDGE,"E0")])],"isStart":false});
            var Q1;
            Q1=makeQuery(id+"F10.opExtrude","CAP_EDGE",EDGE,{"disambiguationData":[OSD([sQuery(id+"F0.wireOp",EDGE,"E0")])],"isStart":true});
            fillet(context, id + "F17", {"entities" : qUnion([Q0, Q1]), "radius" : 1.5 * mm, "tangentPropagation" : true, "allowEdgeOverflow" : false});
        }
        {
            var Q0;
            Q0=makeQuery(id+"F1.imprint","IMPRINT",FACE,{"disambiguationData":[TD([[makeQuery(id+"F1.imprint","IMPRINT",EDGE,{"derivedFrom":sQuery(id+"F1.wireOp",EDGE,"E3")}),1.0]])]});
            var Q1;
            Q1=makeQuery(id+"F1.imprint","IMPRINT",FACE,{"disambiguationData":[TD([[makeQuery(id+"F1.imprint","IMPRINT",EDGE,{"derivedFrom":sQuery(id+"F1.wireOp",EDGE,"E9.MirrorCS")}),-1.0]])]});
            extrude(context, id + "F18", {"entities" : qUnion([Q0, Q1]), "operationType" : NewBodyOperationType.REMOVE, "depth" : 40 * mm, "offsetDistance" : 25 * mm, "symmetric" : true});
        }
    });
